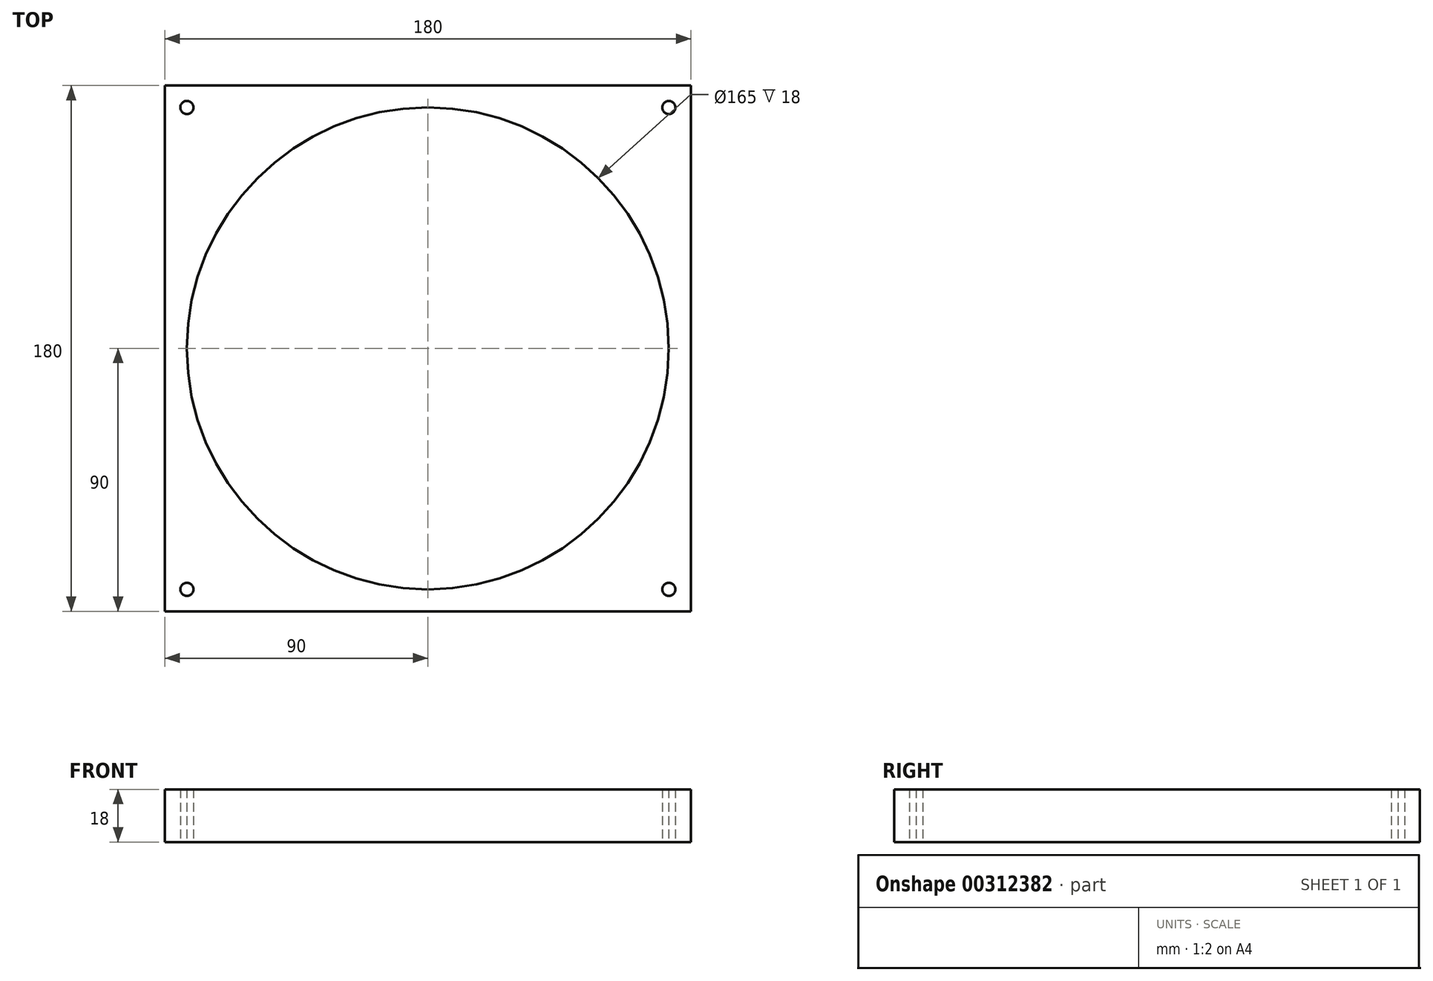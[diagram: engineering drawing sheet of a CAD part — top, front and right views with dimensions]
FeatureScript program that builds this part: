
annotation { "Feature Type Name" : "Feature", "Feature Type Description" : "" }
export const myFeature = defineFeature(function(context is Context, id is Id, definition is map)
    precondition{}
    {
        {
            var Q0;
            Q0=qCreatedBy(makeId("Top.planeOp"),FACE);
            var sketch = newSketch(context, id + "F0", { "sketchPlane" : qUnion([Q0])});
            skLineSegment(sketch, "E0.bottom", {"start": v(90, -90) * mm, "end": v(-90, -90) * mm});
            skLineSegment(sketch, "E0.top", {"start": v(90, 90) * mm, "end": v(-90, 90) * mm});
            skLineSegment(sketch, "E0.left", {"start": v(90, -90) * mm, "end": v(90, 90) * mm});
            skLineSegment(sketch, "E0.right", {"start": v(-90, -90) * mm, "end": v(-90, 90) * mm});
            skPoint(sketch, "E0.middle", {"position": v(0, 0) * mm});
            skLineSegment(sketch, "E1.bottom", {"start": v(82.5, -82.5) * mm, "end": v(-82.5, -82.5) * mm});
            skLineSegment(sketch, "E1.top", {"start": v(82.5, 82.5) * mm, "end": v(-82.5, 82.5) * mm});
            skLineSegment(sketch, "E1.left", {"start": v(82.5, -82.5) * mm, "end": v(82.5, 82.5) * mm});
            skLineSegment(sketch, "E1.right", {"start": v(-82.5, -82.5) * mm, "end": v(-82.5, 82.5) * mm});
            skCircle(sketch, "E2", {"center": v(-82.5, 82.5) * mm, "radius": 2.25 * mm});
            skCircle(sketch, "E3", {"center": v(82.5, 82.5) * mm, "radius": 2.25 * mm});
            skCircle(sketch, "E4", {"center": v(82.5, -82.5) * mm, "radius": 2.25 * mm});
            skCircle(sketch, "E5", {"center": v(-82.5, -82.5) * mm, "radius": 2.25 * mm});
            skCircle(sketch, "E6", {"center": v(0, 0) * mm, "radius": 82.5 * mm});
            skSolve(sketch);
        }
        {
            var Q0;
            Q0 = qSketchRegion(id + "F0", true);
            var Q1;
            {var subQ0=sQuery(id+"F0.wireOp",EDGE,"E6");var subQ1=sQuery(id+"F0.wireOp",EDGE,"E1.bottom");var subQ2=makeQuery(id+"F0.imprint","INTERSECT",VERTEX,{"derivedFrom":[subQ1,subQ0]});Q1=makeQuery(id+"F0.imprint","IMPRINT",FACE,{"disambiguationData":[TD([[makeQuery(id+"F0.imprint","IMPRINT",EDGE,{"disambiguationData":[TD([[subQ2,-1.0]])],"derivedFrom":subQ1}),-1.0]])]});}
            var Q2;
            {var subQ0=sQuery(id+"F0.wireOp",EDGE,"E6");var subQ1=sQuery(id+"F0.wireOp",EDGE,"E1.top");var subQ2=makeQuery(id+"F0.imprint","INTERSECT",VERTEX,{"derivedFrom":[subQ1,subQ0]});Q2=makeQuery(id+"F0.imprint","IMPRINT",FACE,{"disambiguationData":[TD([[makeQuery(id+"F0.imprint","IMPRINT",EDGE,{"disambiguationData":[TD([[subQ2,-1.0]])],"derivedFrom":subQ1}),1.0]])]});}
            var Q3;
            {var subQ0=sQuery(id+"F0.wireOp",EDGE,"E4");var subQ1=sQuery(id+"F0.wireOp",EDGE,"E1.bottom");var subQ2=makeQuery(id+"F0.imprint","INTERSECT",VERTEX,{"derivedFrom":[subQ1,subQ0]});Q3=makeQuery(id+"F0.imprint","IMPRINT",FACE,{"disambiguationData":[TD([[makeQuery(id+"F0.imprint","IMPRINT",EDGE,{"disambiguationData":[TD([[subQ2,-1.0]])],"derivedFrom":subQ1}),-1.0]])]});}
            var Q4;
            {var subQ0=sQuery(id+"F0.wireOp",EDGE,"E3");var subQ1=sQuery(id+"F0.wireOp",EDGE,"E1.top");var subQ2=makeQuery(id+"F0.imprint","INTERSECT",VERTEX,{"derivedFrom":[subQ1,subQ0]});Q4=makeQuery(id+"F0.imprint","IMPRINT",FACE,{"disambiguationData":[TD([[makeQuery(id+"F0.imprint","IMPRINT",EDGE,{"disambiguationData":[TD([[subQ2,-1.0]])],"derivedFrom":subQ1}),1.0]])]});}
            extrude(context, id + "F1", {"entities" : qUnion([Q0, Q1, Q2, Q3, Q4]), "depth" : 18 * mm});
        }
    });
